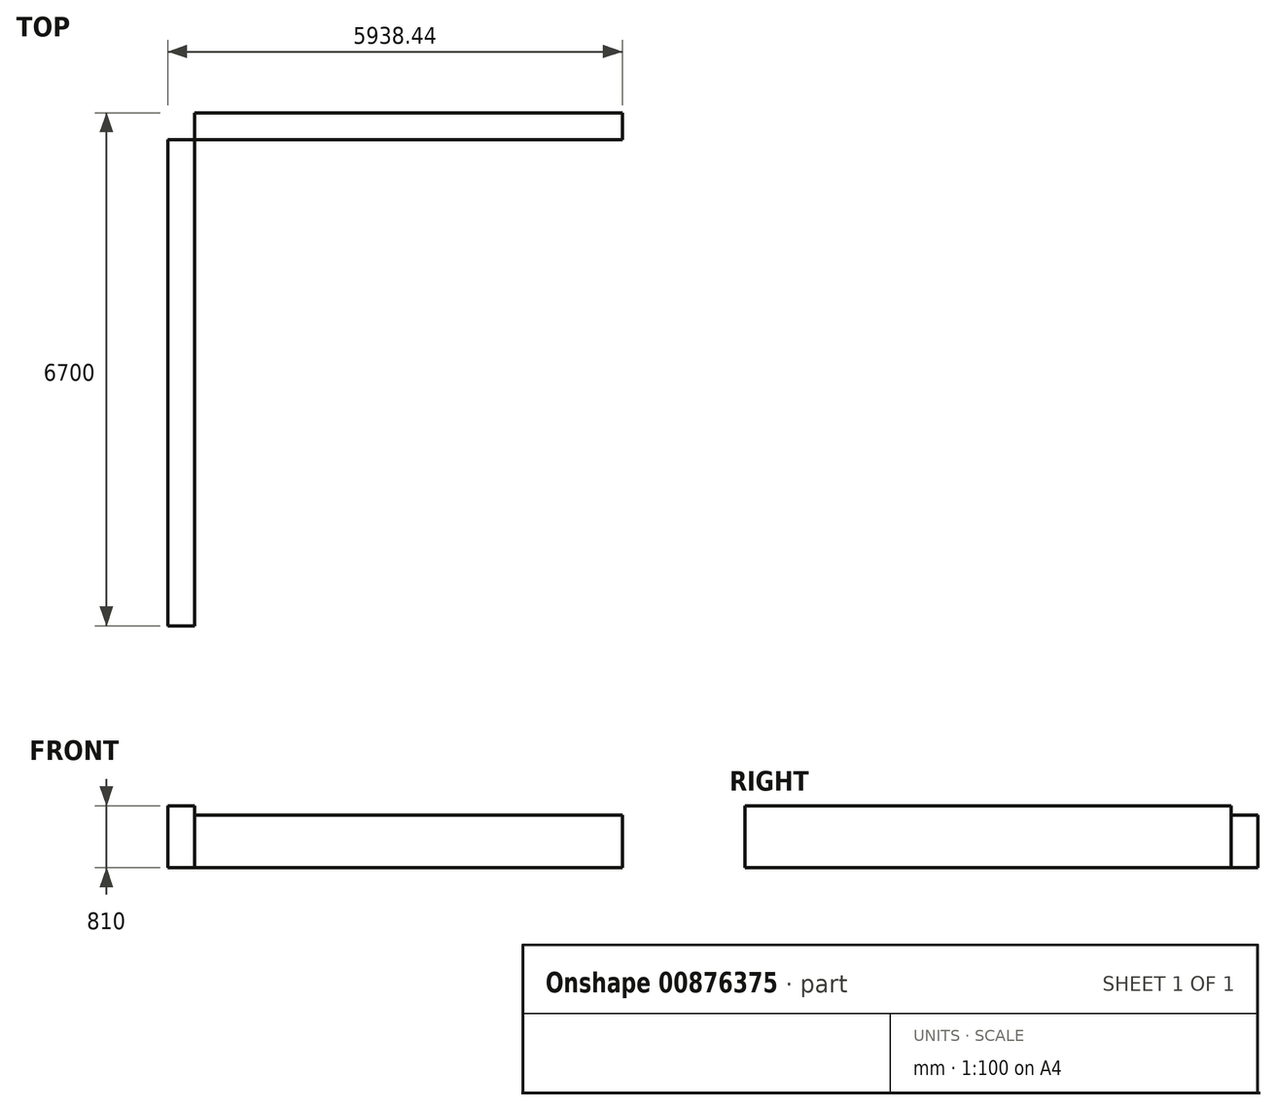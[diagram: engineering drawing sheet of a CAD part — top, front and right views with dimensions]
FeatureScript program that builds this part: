
annotation { "Feature Type Name" : "Feature", "Feature Type Description" : "" }
export const myFeature = defineFeature(function(context is Context, id is Id, definition is map)
    precondition{}
    {
        {
            var Q0;
            Q0=qCreatedBy(makeId("Top.planeOp"),FACE);
            var sketch = newSketch(context, id + "F0", { "sketchPlane" : qUnion([Q0])});
            skLineSegment(sketch, "E0.bottom", {"start": v(0, 0) * mm, "end": v(11000, 0) * mm});
            skLineSegment(sketch, "E0.top", {"start": v(0, 6700) * mm, "end": v(11000, 6700) * mm});
            skLineSegment(sketch, "E0.left", {"start": v(0, 0) * mm, "end": v(0, 6700) * mm});
            skLineSegment(sketch, "E0.right", {"start": v(11000, 0) * mm, "end": v(11000, 6700) * mm});
            skLineSegment(sketch, "E1.bottom", {"start": v(11000, 0) * mm, "end": v(8000, 0) * mm});
            skLineSegment(sketch, "E1.top", {"start": v(11000, 4000) * mm, "end": v(8000, 4000) * mm});
            skLineSegment(sketch, "E1.left", {"start": v(11000, 0) * mm, "end": v(11000, 4000) * mm});
            skLineSegment(sketch, "E1.right", {"start": v(8000, 0) * mm, "end": v(8000, 4000) * mm});
            skLineSegment(sketch, "E2.bottom", {"start": v(11000, 6700) * mm, "end": v(8000, 6700) * mm});
            skLineSegment(sketch, "E2.top", {"start": v(11000, 4100) * mm, "end": v(8000, 4100) * mm});
            skLineSegment(sketch, "E2.left", {"start": v(11000, 6700) * mm, "end": v(11000, 4100) * mm});
            skLineSegment(sketch, "E2.right", {"start": v(8000, 6700) * mm, "end": v(8000, 4100) * mm});
            skLineSegment(sketch, "E3", {"start": v(11000, 6700) * mm, "end": v(8000, 4100) * mm, "construction": true});
            skLineSegment(sketch, "E4", {"start": v(8000, 6700) * mm, "end": v(11000, 4100) * mm, "construction": true});
            skLineSegment(sketch, "E5.bottom", {"start": v(0, 0) * mm, "end": v(1250, 0) * mm});
            skLineSegment(sketch, "E5.top", {"start": v(0, -100) * mm, "end": v(1250, -100) * mm});
            skLineSegment(sketch, "E5.left", {"start": v(0, 0) * mm, "end": v(0, -100) * mm});
            skLineSegment(sketch, "E5.right", {"start": v(1250, 0) * mm, "end": v(1250, -100) * mm});
            skLineSegment(sketch, "E6", {"start": v(1250, 0) * mm, "end": v(1250, 1000) * mm});
            skLineSegment(sketch, "E7", {"start": v(1250, 1000) * mm, "end": v(1250, 0) * mm});
            skLineSegment(sketch, "E8", {"start": v(1250, -1000) * mm, "end": v(1250, 0) * mm});
            skArc(sketch, "E9.trimOffspring", {"start": v(1250, -1000) * mm, "mid": v(2250, 0) * mm, "end": v(1250, 1000) * mm});
            skLineSegment(sketch, "E10.bottom", {"start": v(2250, 0) * mm, "end": v(7285.86, 0) * mm});
            skLineSegment(sketch, "E10.top", {"start": v(2250, -100) * mm, "end": v(11000, -100) * mm});
            skLineSegment(sketch, "E10.left", {"start": v(2250, 0) * mm, "end": v(2250, -100) * mm});
            skLineSegment(sketch, "E10.right", {"start": v(11000, 0) * mm, "end": v(11000, -100) * mm});
            skLineSegment(sketch, "E11", {"start": v(8000, 0) * mm, "end": v(8082.58, -540.15) * mm});
            skLineSegment(sketch, "E12", {"start": v(8082.58, -540.15) * mm, "end": v(8169.81, -49.45) * mm});
            skLineSegment(sketch, "E13", {"start": v(8169.81, -49.45) * mm, "end": v(8235.24, -540.15) * mm});
            skLineSegment(sketch, "E14", {"start": v(11000, 0) * mm, "end": v(10895.91, -529.24) * mm});
            skLineSegment(sketch, "E15", {"start": v(10895.91, -529.24) * mm, "end": v(10808.68, 0) * mm});
            skLineSegment(sketch, "E16", {"start": v(10808.68, 0) * mm, "end": v(10808.68, -529.24) * mm});
            skLineSegment(sketch, "E17", {"start": v(350, 6700) * mm, "end": v(350, 0) * mm});
            skLineSegment(sketch, "E18.bottom", {"start": v(0, 6700) * mm, "end": v(6844.73, 6700) * mm});
            skLineSegment(sketch, "E18.top", {"start": v(0, 6350) * mm, "end": v(6844.73, 6350) * mm});
            skLineSegment(sketch, "E18.left", {"start": v(0, 6700) * mm, "end": v(0, 6350) * mm});
            skLineSegment(sketch, "E18.right", {"start": v(6844.73, 6700) * mm, "end": v(6844.73, 6350) * mm});
            skLineSegment(sketch, "E19", {"start": v(1327.1, 6700) * mm, "end": v(1327.1, 6350) * mm});
            skLineSegment(sketch, "E20", {"start": v(1995.57, 6700) * mm, "end": v(1995.57, 6350) * mm});
            skLineSegment(sketch, "E21", {"start": v(5039.83, 6700) * mm, "end": v(5039.83, 6350) * mm});
            skLineSegment(sketch, "E22", {"start": v(5938.44, 6700) * mm, "end": v(5938.44, 6350) * mm});
            skArc(sketch, "E23", {"start": v(8000, 1700) * mm, "mid": v(7292.9, 1407.1) * mm, "end": v(7000, 700) * mm});
            skLineSegment(sketch, "E24", {"start": v(8000, 700) * mm, "end": v(7000, 700) * mm});
            skArc(sketch, "E25.trimOffspring", {"start": v(7285.86, 0) * mm, "mid": v(7341.03, -52.17) * mm, "end": v(7400, -100) * mm});
            skArc(sketch, "E26.trimOffspring", {"start": v(8045.7, -298.95) * mm, "mid": v(8123.48, -292.35) * mm, "end": v(8200.51, -279.7) * mm});
            skArc(sketch, "E27.trimOffspring", {"start": v(8600, -100) * mm, "mid": v(8658.97, -52.17) * mm, "end": v(8714.14, 0) * mm});
            skLineSegment(sketch, "E28.trimOffspring", {"start": v(8000, 0) * mm, "end": v(11000, 0) * mm});
            skLineSegment(sketch, "E29.bottom", {"start": v(8000, 1700) * mm, "end": v(8700, 1700) * mm});
            skLineSegment(sketch, "E29.top", {"start": v(8000, 4000) * mm, "end": v(8700, 4000) * mm});
            skLineSegment(sketch, "E29.left", {"start": v(8000, 1700) * mm, "end": v(8000, 4000) * mm});
            skLineSegment(sketch, "E29.right", {"start": v(8700, 1700) * mm, "end": v(8700, 4000) * mm, "construction": true});
            skLineSegment(sketch, "E30.bottom", {"start": v(8000, 4000) * mm, "end": v(11000, 4000) * mm});
            skLineSegment(sketch, "E30.top", {"start": v(8000, 3350) * mm, "end": v(11000, 3350) * mm, "construction": true});
            skLineSegment(sketch, "E30.left", {"start": v(8000, 4000) * mm, "end": v(8000, 3350) * mm});
            skLineSegment(sketch, "E30.right", {"start": v(11000, 4000) * mm, "end": v(11000, 3350) * mm});
            skLineSegment(sketch, "E31.bottom", {"start": v(11000, 4000) * mm, "end": v(10300, 4000) * mm});
            skLineSegment(sketch, "E31.top", {"start": v(11000, 0) * mm, "end": v(10300, 0) * mm});
            skLineSegment(sketch, "E31.left", {"start": v(11000, 4000) * mm, "end": v(11000, 0) * mm});
            skLineSegment(sketch, "E31.right", {"start": v(10300, 4000) * mm, "end": v(10300, 0) * mm, "construction": true});
            skLineSegment(sketch, "E32.top", {"start": v(8000, 700) * mm, "end": v(11000, 700) * mm, "construction": true});
            skLineSegment(sketch, "E32.left", {"start": v(8000, 0) * mm, "end": v(8000, 700) * mm});
            skLineSegment(sketch, "E32.right", {"start": v(11000, 0) * mm, "end": v(11000, 700) * mm});
            skLineSegment(sketch, "E33", {"start": v(8700, 2996.55) * mm, "end": v(10300, 2996.55) * mm});
            skLineSegment(sketch, "E34", {"start": v(9987.52, 3350) * mm, "end": v(9987.52, 700) * mm});
            skLineSegment(sketch, "E35.bottom", {"start": v(8000, 6700) * mm, "end": v(7535.56, 6700) * mm});
            skLineSegment(sketch, "E35.top", {"start": v(8000, 1732.02) * mm, "end": v(7535.56, 1732.02) * mm});
            skLineSegment(sketch, "E35.left", {"start": v(8000, 6700) * mm, "end": v(8000, 1732.02) * mm});
            skLineSegment(sketch, "E35.right", {"start": v(7535.56, 6700) * mm, "end": v(7535.56, 1732.02) * mm});
            skLineSegment(sketch, "E36.bottom", {"start": v(2250, 0) * mm, "end": v(2739.59, 0) * mm});
            skLineSegment(sketch, "E36.top", {"start": v(2250, 1901.65) * mm, "end": v(2739.59, 1901.65) * mm});
            skLineSegment(sketch, "E36.left", {"start": v(2250, 0) * mm, "end": v(2250, 1901.65) * mm});
            skLineSegment(sketch, "E36.right", {"start": v(2739.59, 0) * mm, "end": v(2739.59, 1901.65) * mm});
            skLineSegment(sketch, "E37.bottom", {"start": v(2250, 1901.65) * mm, "end": v(4158.33, 1901.65) * mm});
            skLineSegment(sketch, "E37.top", {"start": v(2250, 1392.75) * mm, "end": v(4158.33, 1392.75) * mm});
            skLineSegment(sketch, "E37.left", {"start": v(2250, 1901.65) * mm, "end": v(2250, 1392.75) * mm});
            skLineSegment(sketch, "E37.right", {"start": v(4158.33, 1901.65) * mm, "end": v(4158.33, 1392.75) * mm});
            skSolve(sketch);
        }
        {
            var Q0;
            {var subQ3=sQuery(id+"F0.wireOp",EDGE,"E17");var subQ5=sQuery(id+"F0.wireOp",EDGE,"E18.top");var subQ6=makeQuery(id+"F0.imprint","INTERSECT",VERTEX,{"derivedFrom":[subQ3,subQ5]});Q0=makeQuery(id+"F0.imprint","IMPRINT",FACE,{"disambiguationData":[TD([[makeQuery(id+"F0.imprint","IMPRINT",EDGE,{"disambiguationData":[TD([[subQ6,-1.0]])],"derivedFrom":subQ3}),-1.0]])]});}
            extrude(context, id + "F1", {"entities" : qUnion([Q0]), "depth" : 810 * mm, "offsetDistance" : 25 * mm});
        }
        {
            var Q0;
            {var subQ0=sQuery(id+"F0.wireOp",EDGE,"E20");Q0=makeQuery(id+"F0.imprint","IMPRINT",FACE,{"disambiguationData":[TD([[makeQuery(id+"F0.imprint","IMPRINT",EDGE,{"derivedFrom":subQ0}),1.0]])]});}
            var Q1;
            {var subQ2=sQuery(id+"F0.wireOp",EDGE,"E19");Q1=makeQuery(id+"F0.imprint","IMPRINT",FACE,{"disambiguationData":[TD([[makeQuery(id+"F0.imprint","IMPRINT",EDGE,{"derivedFrom":subQ2}),1.0]])]});}
            var Q2;
            {var subQ3=sQuery(id+"F0.wireOp",EDGE,"E19");Q2=makeQuery(id+"F0.imprint","IMPRINT",FACE,{"disambiguationData":[TD([[makeQuery(id+"F0.imprint","IMPRINT",EDGE,{"derivedFrom":subQ3}),-1.0]])]});}
            var Q3;
            {var subQ0=sQuery(id+"F0.wireOp",EDGE,"E21");Q3=makeQuery(id+"F0.imprint","IMPRINT",FACE,{"disambiguationData":[TD([[makeQuery(id+"F0.imprint","IMPRINT",EDGE,{"derivedFrom":subQ0}),1.0]])]});}
            extrude(context, id + "F2", {"entities" : qUnion([Q0, Q1, Q2, Q3]), "depth" : 690 * mm, "offsetDistance" : 25 * mm});
        }
    });
